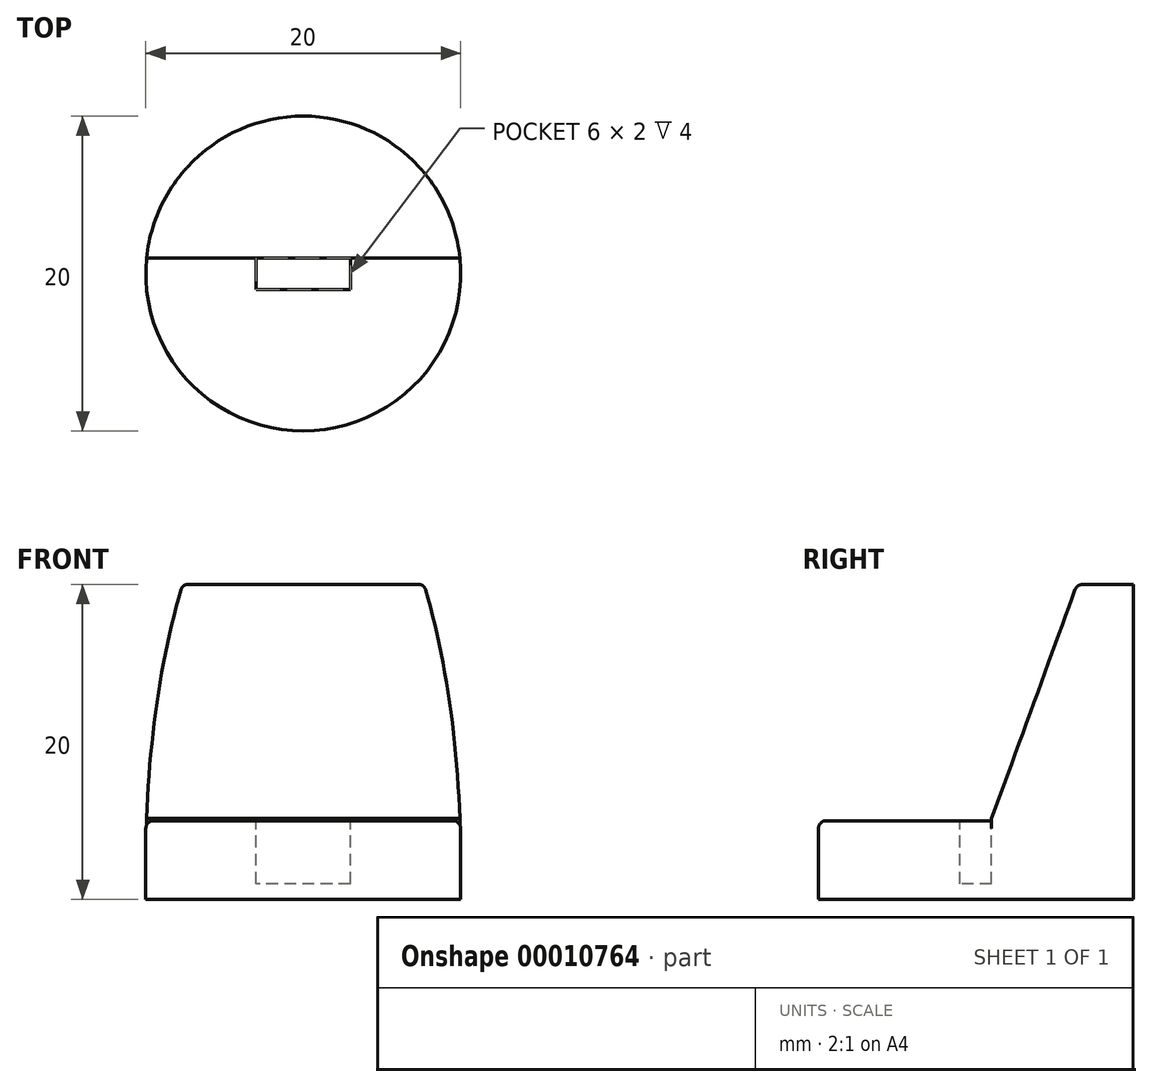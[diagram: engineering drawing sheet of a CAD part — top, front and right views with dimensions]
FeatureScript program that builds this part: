
annotation { "Feature Type Name" : "Feature", "Feature Type Description" : "" }
export const myFeature = defineFeature(function(context is Context, id is Id, definition is map)
    precondition{}
    {
        {
            var Q0;
            Q0=qCreatedBy(makeId("Top.planeOp"),FACE);
            var sketch = newSketch(context, id + "F0", { "sketchPlane" : qUnion([Q0])});
            skCircle(sketch, "E0", {"center": v(0, 0) * mm, "radius": 10 * mm});
            skSolve(sketch);
        }
        {
            var Q0;
            Q0=makeQuery(id+"F0.imprint","IMPRINT",FACE,{"disambiguationData":[TD([[makeQuery(id+"F0.imprint","IMPRINT",EDGE,{"derivedFrom":sQuery(id+"F0.wireOp",EDGE,"E0")}),1.0]])]});
            extrude(context, id + "F1", {"entities" : qUnion([Q0]), "depth" : 5 * mm});
        }
        {
            var Q0;
            Q0=qCreatedBy(makeId("Front.planeOp"),FACE);
            var sketch = newSketch(context, id + "F2", { "sketchPlane" : qUnion([Q0])});
            skLineSegment(sketch, "E1.rect.bottom", {"start": v(3, 1) * mm, "end": v(-3, 1) * mm});
            skLineSegment(sketch, "E1.rect.top", {"start": v(3, 10.8) * mm, "end": v(-3, 10.8) * mm});
            skLineSegment(sketch, "E1.rect.left", {"start": v(3, 1) * mm, "end": v(3, 10.8) * mm});
            skLineSegment(sketch, "E1.rect.right", {"start": v(-3, 1) * mm, "end": v(-3, 10.8) * mm});
            skPoint(sketch, "E1.rect.middle", {"position": v(0, 5.9) * mm});
            skSolve(sketch);
        }
        {
            var Q0;
            Q0=makeQuery(id+"F2.imprint","IMPRINT",FACE,{"disambiguationData":[TD([[makeQuery(id+"F2.imprint","IMPRINT",EDGE,{"derivedFrom":sQuery(id+"F2.wireOp",EDGE,"E1.rect.bottom")}),-1.0]])]});
            extrude(context, id + "F3", {"entities" : qUnion([Q0]), "operationType" : NewBodyOperationType.REMOVE, "endBound" : BoundingType.SYMMETRIC, "oppositeDirection" : true, "depth" : 2 * mm});
        }
        {
            var Q0;
            Q0=makeQuery(id+"F1.opExtrude","CAP_FACE",FACE,{"disambiguationData":[OSD([sQuery(id+"F0.wireOp",EDGE,"E0")])],"isStart":false});
            var sketch = newSketch(context, id + "F4", { "sketchPlane" : qUnion([Q0])});
            skLineSegment(sketch, "E2", {"start": v(-9.95, 1) * mm, "end": v(9.95, 1) * mm});
            skSolve(sketch);
        }
        {
            var Q0;
            {var subQ0=sQuery(id+"F0.wireOp",EDGE,"E0");var subQ1=makeQuery(id+"F1.opExtrude","CAP_EDGE",EDGE,{"disambiguationData":[OSD([subQ0])],"isStart":false});var subQ2=sQuery(id+"F4.wireOp",EDGE,"E2");var subQ4=makeQuery(id+"F4.imprint","INTERSECT",VERTEX,{"disambiguationData":[OD(0.0)],"derivedFrom":[subQ1,subQ2]});Q0=makeQuery(id+"F4.imprint","IMPRINT",FACE,{"disambiguationData":[TD([[makeQuery(id+"F4.imprint","IMPRINT",EDGE,{"disambiguationData":[TD([[subQ4,1.0]])],"derivedFrom":subQ1}),1.0]])]});}
            extrude(context, id + "F5", {"entities" : qUnion([Q0]), "operationType" : NewBodyOperationType.ADD, "depth" : 15 * mm});
        }
        {
            var Q0;
            Q0=qCreatedBy(makeId("Right.planeOp"),FACE);
            var sketch = newSketch(context, id + "F6", { "sketchPlane" : qUnion([Q0])});
            skLineSegment(sketch, "E3", {"start": v(0.97, 5.05) * mm, "end": v(7.15, 22) * mm});
            skLineSegment(sketch, "E4", {"start": v(7.15, 22) * mm, "end": v(0.96, 22) * mm});
            skLineSegment(sketch, "E5", {"start": v(0.96, 22) * mm, "end": v(0.97, 5.05) * mm});
            skSolve(sketch);
        }
        {
            var Q0;
            Q0 = qSketchRegion(id + "F6", true);
            extrude(context, id + "F7", {"entities" : qUnion([Q0]), "operationType" : NewBodyOperationType.REMOVE, "endBound" : BoundingType.SYMMETRIC, "oppositeDirection" : true, "depth" : 25 * mm});
        }
        {
            var Q0;
            Q0=makeQuery(id+"F1.opExtrude","CAP_EDGE",EDGE,{"disambiguationData":[OSD([sQuery(id+"F0.wireOp",EDGE,"E0")])],"isStart":false});
            fillet(context, id + "F8", {"entities" : qUnion([Q0]), "radius" : .5 * mm, "tangentPropagation" : true, "allowEdgeOverflow" : false});
        }
        {
            var Q0;
            Q0=makeQuery(id+"F7.boolean.opBoolean","INTERSECT",EDGE,{"derivedFrom":[makeQuery(id+"F5.opExtrude","CAP_FACE",FACE,{"disambiguationData":[OSD([sQuery(id+"F0.wireOp",EDGE,"E0"),sQuery(id+"F4.wireOp",EDGE,"E2")])],"isStart":false}),makeQuery(id+"F7.opExtrude","SWEPT_FACE",FACE,{"disambiguationData":[OSD([sQuery(id+"F6.wireOp",EDGE,"E3")])]})]});
            fillet(context, id + "F9", {"entities" : qUnion([Q0]), "radius" : .5 * mm, "tangentPropagation" : true, "allowEdgeOverflow" : false});
        }
    });
